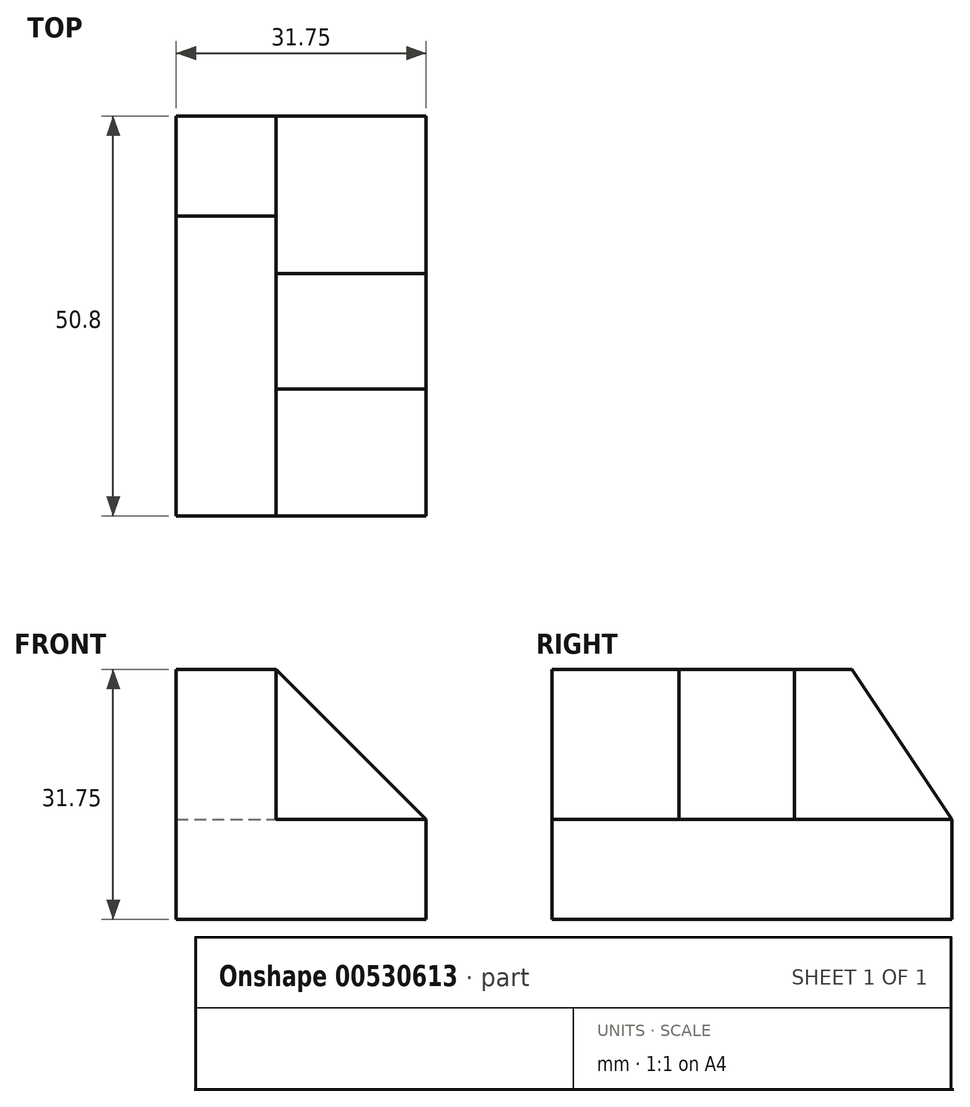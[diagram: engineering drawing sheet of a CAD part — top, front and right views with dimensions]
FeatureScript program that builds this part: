
annotation { "Feature Type Name" : "Feature", "Feature Type Description" : "" }
export const myFeature = defineFeature(function(context is Context, id is Id, definition is map)
    precondition{}
    {
        {
            var Q0;
            Q0=qCreatedBy(makeId("Front.planeOp"),FACE);
            var sketch = newSketch(context, id + "F0", { "sketchPlane" : qUnion([Q0])});
            skLineSegment(sketch, "E0", {"start": v(-54.76, 37.53) * mm, "end": v(-54.76, 5.78) * mm});
            skLineSegment(sketch, "E1", {"start": v(-54.76, 5.78) * mm, "end": v(-23, 5.78) * mm});
            skLineSegment(sketch, "E2", {"start": v(-23, 5.78) * mm, "end": v(-23, 18.48) * mm});
            skLineSegment(sketch, "E3", {"start": v(-23, 18.48) * mm, "end": v(-42.06, 18.48) * mm});
            skLineSegment(sketch, "E4", {"start": v(-42.06, 18.48) * mm, "end": v(-42.06, 37.53) * mm});
            skLineSegment(sketch, "E5", {"start": v(-42.06, 37.53) * mm, "end": v(-54.76, 37.53) * mm});
            skSolve(sketch);
        }
        {
            var Q0;
            Q0=makeQuery(id+"F0.imprint","IMPRINT",FACE,{"disambiguationData":[TD([[makeQuery(id+"F0.imprint","IMPRINT",EDGE,{"derivedFrom":sQuery(id+"F0.wireOp",EDGE,"E0")}),1.0]])]});
            extrude(context, id + "F1", {"entities" : qUnion([Q0]), "depth" : 50.8 * mm, "offsetDistance" : 25.4 * mm});
        }
        {
            var Q0;
            Q0=makeQuery(id+"F1.opExtrude","SWEPT_FACE",FACE,{"disambiguationData":[OSD([sQuery(id+"F0.wireOp",EDGE,"E4")])]});
            var sketch = newSketch(context, id + "F2", { "sketchPlane" : qUnion([Q0])});
            skLineSegment(sketch, "E6", {"start": v(-12.7, 37.53) * mm, "end": v(0, 18.48) * mm});
            skSolve(sketch);
        }
        {
            var Q0;
            {var subQ0=sQuery(id+"F2.wireOp",EDGE,"E6");Q0=makeQuery(id+"F2.imprint","IMPRINT",FACE,{"disambiguationData":[TD([[makeQuery(id+"F2.imprint","IMPRINT",EDGE,{"derivedFrom":subQ0}),1.0]])]});}
            extrude(context, id + "F3", {"entities" : qUnion([Q0]), "operationType" : NewBodyOperationType.REMOVE, "endBound" : BoundingType.THROUGH_ALL, "oppositeDirection" : true, "depth" : 25.4 * mm, "offsetDistance" : 25.4 * mm});
        }
        {
            var Q0;
            Q0=makeQuery(id+"F1.opExtrude","SWEPT_FACE",FACE,{"disambiguationData":[OSD([sQuery(id+"F0.wireOp",EDGE,"E3")])]});
            var sketch = newSketch(context, id + "F4", { "sketchPlane" : qUnion([Q0])});
            skLineSegment(sketch, "E7", {"start": v(-23, -34.68) * mm, "end": v(-42.06, -34.68) * mm});
            skLineSegment(sketch, "E8", {"start": v(-42.06, -20) * mm, "end": v(-23, -20) * mm});
            skSolve(sketch);
        }
        {
            var Q0;
            {var subQ0=sQuery(id+"F4.wireOp",EDGE,"E7");Q0=makeQuery(id+"F4.imprint","IMPRINT",FACE,{"disambiguationData":[TD([[makeQuery(id+"F4.imprint","IMPRINT",EDGE,{"derivedFrom":subQ0}),-1.0]])]});}
            extrude(context, id + "F5", {"entities" : qUnion([Q0]), "operationType" : NewBodyOperationType.ADD, "depth" : 19.05 * mm, "offsetDistance" : 25.4 * mm});
        }
        {
            var Q0;
            Q0=makeQuery(id+"F5.opExtrude","SWEPT_FACE",FACE,{"disambiguationData":[OSD([sQuery(id+"F4.wireOp",EDGE,"E8")])]});
            var sketch = newSketch(context, id + "F6", { "sketchPlane" : qUnion([Q0])});
            skLineSegment(sketch, "E9", {"start": v(42.06, 37.53) * mm, "end": v(23, 18.48) * mm});
            skSolve(sketch);
        }
        {
            var Q0;
            Q0=makeQuery(id+"F6.imprint","IMPRINT",FACE,{"disambiguationData":[TD([[makeQuery(id+"F6.imprint","IMPRINT",EDGE,{"derivedFrom":sQuery(id+"F6.wireOp",EDGE,"E9")}),-1.0]])]});
            extrude(context, id + "F7", {"entities" : qUnion([Q0]), "operationType" : NewBodyOperationType.REMOVE, "endBound" : BoundingType.THROUGH_ALL, "oppositeDirection" : true, "depth" : 25.4 * mm, "offsetDistance" : 25.4 * mm});
        }
    });
